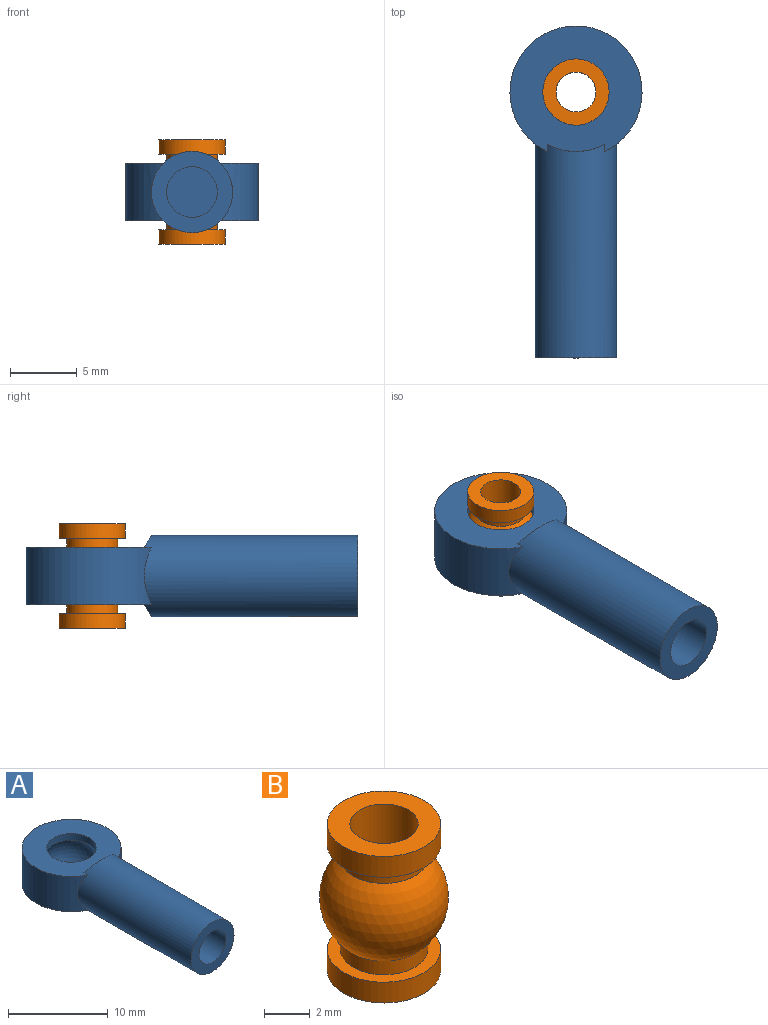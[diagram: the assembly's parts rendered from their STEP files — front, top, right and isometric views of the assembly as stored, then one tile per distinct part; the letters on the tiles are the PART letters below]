
ASSEMBLY  parts=2 mates=1
PART A: 12 faces, bbox 9.9x24.9x6.1 mm
  f0: cylinder r=2.49mm len=4.98mm, axis (0,0,-1), area 12.6mm2, adj f6,f11
  f1: cylinder r=2.49mm len=4.98mm, axis (0,0,-1), area 12.6mm2, adj f5,f11
  f2: cylinder r=3.05mm len=16.06mm, axis (0,1,0), area 302.1mm2, adj f3,f4,f5,f6,f7,f8
  f3: plane 6.1x6.1mm, normal (0,-1,0), area 17.8mm2, adj f2,f9
  f4: cylinder r=4.97mm len=9.93mm, axis (0,0,-1), area 109.3mm2, adj f2,f5,f6
  f5: plane 9.93x9.44mm, normal (0,0,1), area 55.8mm2, adj f1,f2,f4,f7
  f6: plane 9.93x9.44mm, normal (0,0,-1), area 55.8mm2, adj f0,f2,f4,f8
  f7: cylinder r=4.47mm len=4.3mm, axis (0,0,-1), area 2.7mm2, adj f2,f5
  f8: cylinder r=4.47mm len=4.3mm, axis (0,0,1), area 2.7mm2, adj f2,f6
  f9: cylinder r=1.91mm len=9.93mm, axis (0,-1,0), area 118.9mm2, adj f3,f10
  f10: plane 3.81x3.81mm, normal (0,-1,0), area 11.4mm2, adj f9
  f11: sphere r=2.83mm, area 48.1mm2, adj f0,f1
PART B: 10 faces, bbox 5.7x5.7x7.9 mm
  f0: plane 4.98x4.98mm, normal (0,0,-1), area 7.9mm2, adj f1,f9
  f1: cylinder r=2.49mm len=4.98mm, axis (0,0,1), area 17.5mm2, adj f0,f2
  f2: plane 4.98x4.98mm, normal (0,0,1), area 12.4mm2, adj f1,f3
  f3: cylinder r=1.5mm len=7.87mm, axis (0,0,1), area 74.1mm2, adj f2,f4
  f4: plane 4.98x4.98mm, normal (0,0,-1), area 12.4mm2, adj f3,f5
  f5: cylinder r=2.49mm len=4.98mm, axis (0,0,1), area 17.5mm2, adj f4,f6
  f6: plane 4.98x4.98mm, normal (0,0,1), area 7.9mm2, adj f5,f7
  f7: cylinder r=1.92mm len=3.84mm, axis (0,0,1), area 8.9mm2, adj f6,f8
  f8: sphere r=2.83mm, area 74.2mm2, adj f7,f9
  f9: cylinder r=1.92mm len=3.84mm, axis (0,0,1), area 8.9mm2, adj f0,f8
PLACE A t=(-1.9,6.62,0.31)mm
PLACE B t=(-1.9,6.62,0.31)mm
MATE ball B.f1 <-> A.f0  axis (0,0,1) through (-1.9,6.62,0.31)mm
